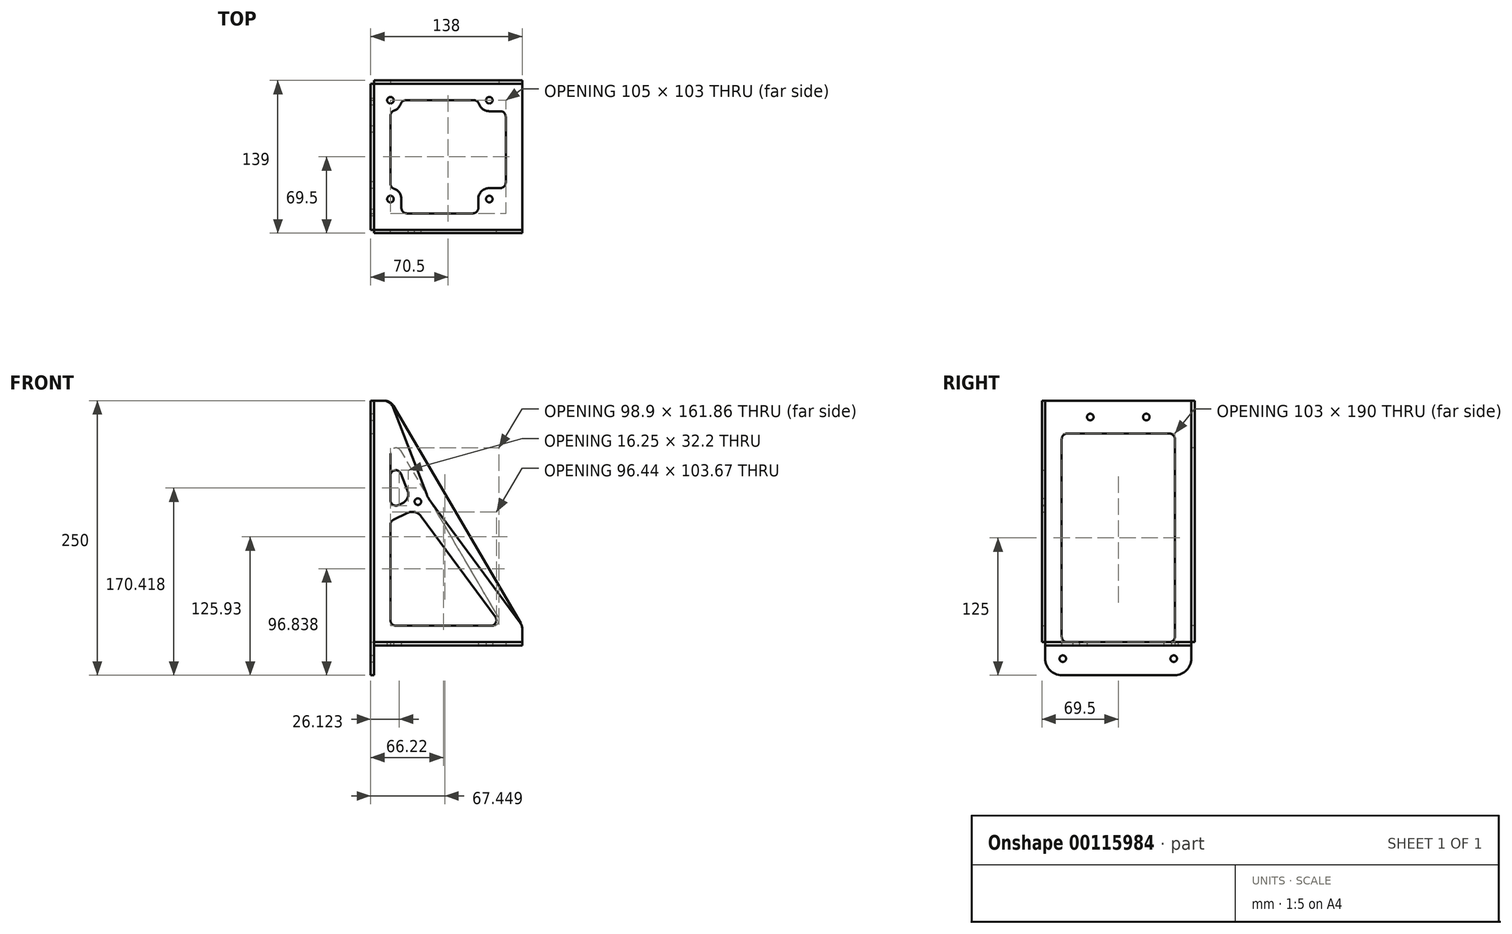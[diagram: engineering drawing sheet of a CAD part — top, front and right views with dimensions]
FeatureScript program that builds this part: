
annotation { "Feature Type Name" : "Feature", "Feature Type Description" : "" }
export const myFeature = defineFeature(function(context is Context, id is Id, definition is map)
    precondition{}
    {
        {
            var Q0;
            Q0=qCreatedBy(makeId("Top.planeOp"),FACE);
            var sketch = newSketch(context, id + "F0", { "sketchPlane" : qUnion([Q0])});
            skCircle(sketch, "E0", {"center": v(0, 0) * mm, "radius": 3 * mm});
            skCircle(sketch, "E1", {"center": v(0, 90) * mm, "radius": 3 * mm});
            skCircle(sketch, "E2", {"center": v(90, 0) * mm, "radius": 3 * mm});
            skCircle(sketch, "E3", {"center": v(90, 90) * mm, "radius": 3 * mm});
            skArc(sketch, "E4", {"start": v(3.33, 80.57) * mm, "mid": v(7.07, 82.93) * mm, "end": v(9.43, 86.67) * mm});
            skArc(sketch, "E5", {"start": v(80.57, 86.67) * mm, "mid": v(84.23, 81.84) * mm, "end": v(90, 80) * mm});
            skArc(sketch, "E6", {"start": v(90, 10) * mm, "mid": v(82.93, 7.07) * mm, "end": v(80, 0) * mm});
            skArc(sketch, "E7", {"start": v(10, 0) * mm, "mid": v(8.16, 5.77) * mm, "end": v(3.33, 9.43) * mm});
            skLineSegment(sketch, "E8.bottom", {"start": v(-15, 105) * mm, "end": v(120, 105) * mm});
            skLineSegment(sketch, "E8.top", {"start": v(-15, -28) * mm, "end": v(120, -28) * mm});
            skLineSegment(sketch, "E8.left", {"start": v(-15, 105) * mm, "end": v(-15, -28) * mm});
            skLineSegment(sketch, "E8.right", {"start": v(120, 105) * mm, "end": v(120, -28) * mm});
            skLineSegment(sketch, "E9", {"start": v(0, 75.86) * mm, "end": v(0, 14.14) * mm});
            skLineSegment(sketch, "E10", {"start": v(15, -13) * mm, "end": v(75, -13) * mm});
            skLineSegment(sketch, "E11", {"start": v(75.86, 90) * mm, "end": v(14.14, 90) * mm});
            skPoint(sketch, "E12.orphan", {"position": v(0, 80) * mm});
            skPoint(sketch, "E13.orphan", {"position": v(80, 90) * mm});
            skPoint(sketch, "E14.orphan", {"position": v(0, -10) * mm});
            skArc(sketch, "E15.filletArc", {"start": v(3.33, 80.57) * mm, "mid": v(0.92, 78.74) * mm, "end": v(0, 75.86) * mm});
            skPoint(sketch, "E16.visualSharp", {"position": v(10, 90) * mm});
            skArc(sketch, "E16.filletArc", {"start": v(14.14, 90) * mm, "mid": v(11.26, 89.08) * mm, "end": v(9.43, 86.67) * mm});
            skArc(sketch, "E17.filletArc", {"start": v(80.57, 86.67) * mm, "mid": v(78.74, 89.08) * mm, "end": v(75.86, 90) * mm});
            skPoint(sketch, "E18.visualSharp", {"position": v(0, 10) * mm});
            skArc(sketch, "E18.filletArc", {"start": v(0, 14.14) * mm, "mid": v(0.92, 11.26) * mm, "end": v(3.33, 9.43) * mm});
            skPoint(sketch, "E19.start.orphan", {"position": v(90, -13) * mm});
            skLineSegment(sketch, "E20", {"start": v(105, 75) * mm, "end": v(105, 15) * mm});
            skLineSegment(sketch, "E21", {"start": v(10, 0) * mm, "end": v(10, -8) * mm});
            skPoint(sketch, "E22.visualSharp", {"position": v(10, -13) * mm});
            skArc(sketch, "E22.filletArc", {"start": v(10, -8) * mm, "mid": v(11.46, -11.54) * mm, "end": v(15, -13) * mm});
            skLineSegment(sketch, "E23", {"start": v(80, 0) * mm, "end": v(80, -8) * mm});
            skPoint(sketch, "E24.visualSharp", {"position": v(80, -13) * mm});
            skArc(sketch, "E24.filletArc", {"start": v(75, -13) * mm, "mid": v(78.54, -11.54) * mm, "end": v(80, -8) * mm});
            skLineSegment(sketch, "E25", {"start": v(90, 10) * mm, "end": v(100, 10) * mm});
            skPoint(sketch, "E26.visualSharp", {"position": v(105, 10) * mm});
            skArc(sketch, "E26.filletArc", {"start": v(100, 10) * mm, "mid": v(103.54, 11.46) * mm, "end": v(105, 15) * mm});
            skLineSegment(sketch, "E27", {"start": v(90, 80) * mm, "end": v(100, 80) * mm});
            skPoint(sketch, "E28.visualSharp", {"position": v(105, 80) * mm});
            skArc(sketch, "E28.filletArc", {"start": v(105, 75) * mm, "mid": v(103.54, 78.54) * mm, "end": v(100, 80) * mm});
            skSolve(sketch);
        }
        {
            var Q0;
            Q0=qSketchRegion(id+"F0",true);
            extrude(context, id + "F1", {"entities" : qUnion([Q0]), "depth" : 3 * mm});
        }
        {
            var Q0;
            Q0=makeQuery(id+"F1.opExtrude","SWEPT_FACE",FACE,{"disambiguationData":[OSD([sQuery(id+"F0.wireOp",EDGE,"E8.left")])]});
            var sketch = newSketch(context, id + "F2", { "sketchPlane" : qUnion([Q0])});
            skLineSegment(sketch, "E29.0", {"start": v(-85, 3) * mm, "end": v(8, 3) * mm, "construction": true});
            skCircle(sketch, "E30", {"center": v(-89, -12) * mm, "radius": 3 * mm});
            skCircle(sketch, "E31", {"center": v(12, -12) * mm, "radius": 3 * mm});
            skCircle(sketch, "E32", {"center": v(-13, 208) * mm, "radius": 3 * mm});
            skLineSegment(sketch, "E33.top", {"start": v(-105, 223) * mm, "end": v(28, 223) * mm});
            skLineSegment(sketch, "E33.left", {"start": v(-105, 3) * mm, "end": v(-105, 223) * mm});
            skLineSegment(sketch, "E33.right", {"start": v(28, 3) * mm, "end": v(28, 223) * mm});
            skLineSegment(sketch, "E34", {"start": v(-85, 3) * mm, "end": v(8, 3) * mm});
            skLineSegment(sketch, "E35", {"start": v(13, 8) * mm, "end": v(13, 188) * mm});
            skLineSegment(sketch, "E36", {"start": v(-90, 188) * mm, "end": v(-90, 8) * mm});
            skPoint(sketch, "E37.newPointB", {"position": v(-105, 3) * mm});
            skArc(sketch, "E37.filletArc", {"start": v(-90, 8) * mm, "mid": v(-88.54, 4.46) * mm, "end": v(-85, 3) * mm});
            skPoint(sketch, "E38.newPointB", {"position": v(28, 3) * mm});
            skArc(sketch, "E38.filletArc", {"start": v(8, 3) * mm, "mid": v(11.54, 4.46) * mm, "end": v(13, 8) * mm});
            skPoint(sketch, "E39.orphan", {"position": v(-90, 3) * mm});
            skLineSegment(sketch, "E40", {"start": v(-105, 3) * mm, "end": v(-105, -12) * mm});
            skLineSegment(sketch, "E41", {"start": v(-90, -27) * mm, "end": v(13, -27) * mm});
            skLineSegment(sketch, "E42", {"start": v(28, -12) * mm, "end": v(28, 3) * mm});
            skPoint(sketch, "E43.visualSharp", {"position": v(-105, -27) * mm});
            skArc(sketch, "E43.filletArc", {"start": v(-105, -12) * mm, "mid": v(-100.6, -22.6) * mm, "end": v(-90, -27) * mm});
            skPoint(sketch, "E44.visualSharp", {"position": v(28, -27) * mm});
            skArc(sketch, "E44.filletArc", {"start": v(13, -27) * mm, "mid": v(23.6, -22.6) * mm, "end": v(28, -12) * mm});
            skCircle(sketch, "E45", {"center": v(-64, 208) * mm, "radius": 3 * mm});
            skLineSegment(sketch, "E46", {"start": v(-85, 193) * mm, "end": v(8, 193) * mm});
            skPoint(sketch, "E47.visualSharp", {"position": v(-90, 193) * mm});
            skArc(sketch, "E47.filletArc", {"start": v(-85, 193) * mm, "mid": v(-88.54, 191.54) * mm, "end": v(-90, 188) * mm});
            skPoint(sketch, "E48.visualSharp", {"position": v(13, 193) * mm});
            skArc(sketch, "E48.filletArc", {"start": v(13, 188) * mm, "mid": v(11.54, 191.54) * mm, "end": v(8, 193) * mm});
            skSolve(sketch);
        }
        {
            var Q0;
            Q0=qSketchRegion(id+"F2",true);
            extrude(context, id + "F3", {"entities" : qUnion([Q0]), "depth" : 3 * mm});
        }
        {
            var Q0;
            Q0=makeQuery(id+"F1.opExtrude","SWEPT_FACE",FACE,{"disambiguationData":[OSD([sQuery(id+"F0.wireOp",EDGE,"E8.bottom")])]});
            var sketch = newSketch(context, id + "F4", { "sketchPlane" : qUnion([Q0])});
            skLineSegment(sketch, "E49.0", {"start": v(15, 3) * mm, "end": v(-120, 3) * mm});
            skLineSegment(sketch, "E50.0", {"start": v(15, 223) * mm, "end": v(15, 223) * mm});
            skLineSegment(sketch, "E51", {"start": v(15, 223) * mm, "end": v(5.73, 223) * mm});
            skLineSegment(sketch, "E52", {"start": v(-2.9, 218.05) * mm, "end": v(-118.63, 20.34) * mm});
            skLineSegment(sketch, "E53", {"start": v(-120, 15.29) * mm, "end": v(-120, 3) * mm});
            skPoint(sketch, "E54.visualSharp", {"position": v(0, 223) * mm});
            skArc(sketch, "E54.filletArc", {"start": v(5.73, 223) * mm, "mid": v(0.76, 221.68) * mm, "end": v(-2.9, 218.05) * mm});
            skPoint(sketch, "E55.visualSharp", {"position": v(-120, 18) * mm});
            skArc(sketch, "E55.filletArc", {"start": v(-118.63, 20.34) * mm, "mid": v(-119.65, 17.9) * mm, "end": v(-120, 15.29) * mm});
            skLineSegment(sketch, "E56", {"start": v(-93.9, 18) * mm, "end": v(-5, 18) * mm});
            skLineSegment(sketch, "E57", {"start": v(0, 23) * mm, "end": v(0, 174.87) * mm});
            skLineSegment(sketch, "E58", {"start": v(-9.32, 177.4) * mm, "end": v(-98.21, 25.53) * mm});
            skPoint(sketch, "E59.visualSharp", {"position": v(0, 193.3) * mm});
            skArc(sketch, "E59.filletArc", {"start": v(0, 174.87) * mm, "mid": v(-3.7, 179.7) * mm, "end": v(-9.32, 177.4) * mm});
            skPoint(sketch, "E60.visualSharp", {"position": v(-102.62, 18) * mm});
            skArc(sketch, "E60.filletArc", {"start": v(-98.21, 25.53) * mm, "mid": v(-98.24, 20.51) * mm, "end": v(-93.9, 18) * mm});
            skPoint(sketch, "E61.visualSharp", {"position": v(0, 18) * mm});
            skArc(sketch, "E61.filletArc", {"start": v(-5, 18) * mm, "mid": v(-1.46, 19.46) * mm, "end": v(0, 23) * mm});
            skLineSegment(sketch, "E62.0", {"start": v(15, 223) * mm, "end": v(15, -12) * mm});
            skSolve(sketch);
        }
        {
            var Q0;
            Q0=qSketchRegion(id+"F4",true);
            extrude(context, id + "F5", {"entities" : qUnion([Q0]), "depth" : 3 * mm});
        }
        {
            var Q0;
            Q0=makeQuery(id+"F1.opExtrude","SWEPT_FACE",FACE,{"disambiguationData":[OSD([sQuery(id+"F0.wireOp",EDGE,"E8.top")])]});
            var sketch = newSketch(context, id + "F6", { "sketchPlane" : qUnion([Q0])});
            skLineSegment(sketch, "E63.0", {"start": v(-15, 3) * mm, "end": v(120, 3) * mm});
            skLineSegment(sketch, "E64.0", {"start": v(-15, 223) * mm, "end": v(-15, 223) * mm});
            skCircle(sketch, "E65", {"center": v(25, 131) * mm, "radius": 3 * mm});
            skCircle(sketch, "E66", {"center": v(25, 131) * mm, "radius": 10 * mm, "construction": true});
            skArc(sketch, "E67", {"start": v(32.92, 137.83) * mm, "mid": v(34.6, 134.2) * mm, "end": v(36.76, 130.83) * mm});
            skLineSegment(sketch, "E68", {"start": v(-15, 223) * mm, "end": v(-6.86, 223) * mm});
            skLineSegment(sketch, "E69", {"start": v(2.47, 216.6) * mm, "end": v(32.92, 137.83) * mm});
            skLineSegment(sketch, "E70", {"start": v(120, 3) * mm, "end": v(120, 14.71) * mm});
            skLineSegment(sketch, "E71", {"start": v(118.05, 20.65) * mm, "end": v(36.76, 130.83) * mm});
            skLineSegment(sketch, "E72", {"start": v(60.9, 148.64) * mm, "end": v(-15, 111.34) * mm, "construction": true});
            skLineSegment(sketch, "E73.trimOffspring", {"start": v(34.37, 134.07) * mm, "end": v(33.54, 135.2) * mm});
            skLineSegment(sketch, "E74.trimOffspring", {"start": v(33.87, 135.36) * mm, "end": v(34.37, 134.07) * mm});
            skPoint(sketch, "E75.visualSharp", {"position": v(120, 18) * mm});
            skArc(sketch, "E75.filletArc", {"start": v(120, 14.71) * mm, "mid": v(119.5, 17.84) * mm, "end": v(118.05, 20.65) * mm});
            skPoint(sketch, "E76.visualSharp", {"position": v(0, 223) * mm});
            skArc(sketch, "E76.filletArc", {"start": v(2.47, 216.6) * mm, "mid": v(-1.2, 221.25) * mm, "end": v(-6.86, 223) * mm});
            skLineSegment(sketch, "E77", {"start": v(7.2, 127.83) * mm, "end": v(11.35, 129.86) * mm});
            skLineSegment(sketch, "E78", {"start": v(2.8, 114.52) * mm, "end": v(15.3, 120.66) * mm});
            skLineSegment(sketch, "E79", {"start": v(0, 154.58) * mm, "end": v(0, 132.31) * mm});
            skLineSegment(sketch, "E80", {"start": v(5, 18) * mm, "end": v(91.46, 18) * mm});
            skLineSegment(sketch, "E81", {"start": v(95.48, 25.97) * mm, "end": v(27.89, 117.59) * mm});
            skLineSegment(sketch, "E82", {"start": v(9.66, 156.38) * mm, "end": v(15.66, 140.88) * mm});
            skLineSegment(sketch, "E83.trimOffspring", {"start": v(20.36, 128.72) * mm, "end": v(21.1, 126.79) * mm});
            skLineSegment(sketch, "E84.trimOffspring", {"start": v(21.1, 126.79) * mm, "end": v(19.86, 128.47) * mm});
            skPoint(sketch, "E85.visualSharp", {"position": v(22.87, 124.38) * mm});
            skArc(sketch, "E85.filletArc", {"start": v(27.89, 117.59) * mm, "mid": v(22.15, 121.4) * mm, "end": v(15.3, 120.66) * mm});
            skLineSegment(sketch, "E86.trimOffspring", {"start": v(119.44, 18) * mm, "end": v(120, 18) * mm});
            skPoint(sketch, "E87.visualSharp", {"position": v(101.36, 18) * mm});
            skArc(sketch, "E87.filletArc", {"start": v(91.46, 18) * mm, "mid": v(95.92, 20.75) * mm, "end": v(95.48, 25.97) * mm});
            skPoint(sketch, "E88.visualSharp", {"position": v(0, 18) * mm});
            skArc(sketch, "E88.filletArc", {"start": v(0, 23) * mm, "mid": v(1.46, 19.46) * mm, "end": v(5, 18) * mm});
            skLineSegment(sketch, "E89.trimOffspring", {"start": v(0, 110.03) * mm, "end": v(0, 23) * mm});
            skPoint(sketch, "E90.visualSharp", {"position": v(0, 113.14) * mm});
            skArc(sketch, "E90.filletArc", {"start": v(2.8, 114.52) * mm, "mid": v(0.76, 112.67) * mm, "end": v(0, 110.03) * mm});
            skPoint(sketch, "E91.visualSharp", {"position": v(0, 181.39) * mm});
            skArc(sketch, "E91.filletArc", {"start": v(9.66, 156.38) * mm, "mid": v(4.08, 159.5) * mm, "end": v(0, 154.58) * mm});
            skPoint(sketch, "E92.visualSharp", {"position": v(0, 124.29) * mm});
            skArc(sketch, "E92.filletArc", {"start": v(0, 132.31) * mm, "mid": v(2.36, 128.07) * mm, "end": v(7.2, 127.83) * mm});
            skPoint(sketch, "E93.visualSharp", {"position": v(18.55, 133.4) * mm});
            skArc(sketch, "E93.filletArc", {"start": v(11.35, 129.86) * mm, "mid": v(15.64, 134.53) * mm, "end": v(15.66, 140.88) * mm});
            skCircle(sketch, "E94", {"center": v(62, 131) * mm, "radius": 20.41 * mm, "construction": true});
            skLineSegment(sketch, "E95.0", {"start": v(-15, -12) * mm, "end": v(-15, 223) * mm});
            skSolve(sketch);
        }
        {
            var Q0;
            Q0=qSketchRegion(id+"F6",true);
            extrude(context, id + "F7", {"entities" : qUnion([Q0]), "depth" : 3 * mm});
        }
    });
